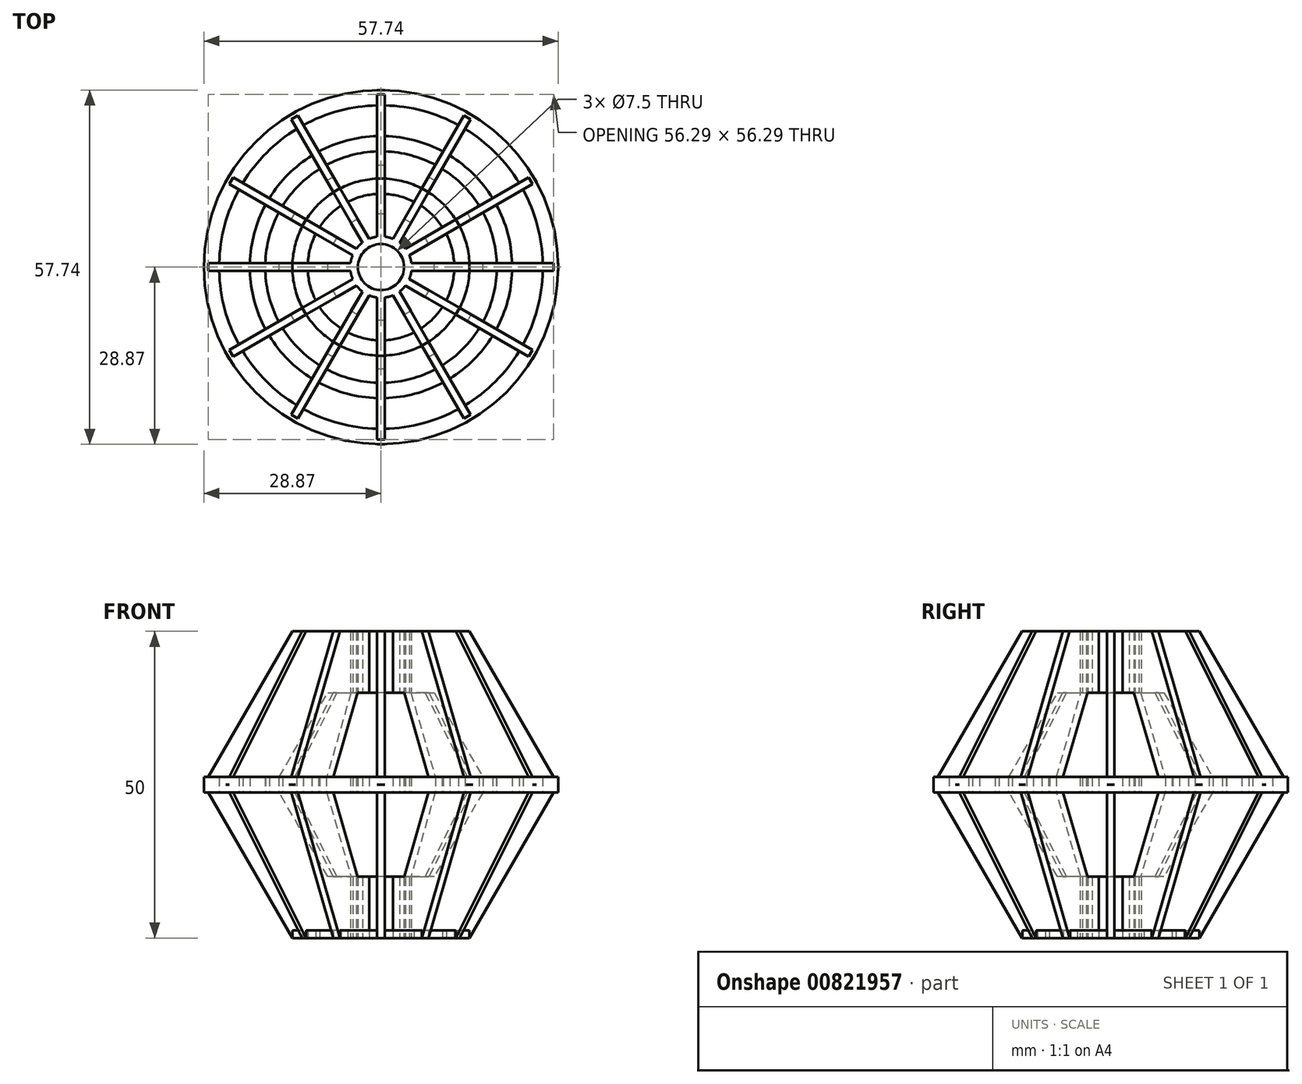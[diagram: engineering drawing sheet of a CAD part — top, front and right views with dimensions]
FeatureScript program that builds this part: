
annotation { "Feature Type Name" : "Feature", "Feature Type Description" : "" }
export const myFeature = defineFeature(function(context is Context, id is Id, definition is map)
    precondition{}
    {
        {
            var Q0;
            Q0=qCreatedBy(makeId("Front.planeOp"),FACE);
            var sketch = newSketch(context, id + "F0", { "sketchPlane" : qUnion([Q0])});
            skCircle(sketch, "E0.cCircle", {"center": v(0, 0) * mm, "radius": 25 * mm, "construction": true});
            skLineSegment(sketch, "E0.0", {"start": v(-14.43, 25) * mm, "end": v(14.43, 25) * mm});
            skLineSegment(sketch, "E0.1", {"start": v(14.43, 25) * mm, "end": v(28.87, 0) * mm});
            skLineSegment(sketch, "E0.2", {"start": v(28.87, 0) * mm, "end": v(14.43, -25) * mm});
            skLineSegment(sketch, "E0.3", {"start": v(14.43, -25) * mm, "end": v(-14.43, -25) * mm});
            skLineSegment(sketch, "E0.4", {"start": v(-14.43, -25) * mm, "end": v(-28.87, 0) * mm});
            skLineSegment(sketch, "E0.5", {"start": v(-28.87, 0) * mm, "end": v(-14.43, 25) * mm});
            skPoint(sketch, "E0.0.midPoint", {"position": v(0, 25) * mm});
            skLineSegment(sketch, "E1", {"start": v(0, 0) * mm, "end": v(0, 13.52) * mm, "construction": true});
            skPoint(sketch, "E2.0.midPoint", {"position": v(0, 13.52) * mm});
            skCircle(sketch, "E3.cCircle", {"center": v(0, 0) * mm, "radius": 15 * mm, "construction": true});
            skLineSegment(sketch, "E3.0", {"start": v(-8.66, 15) * mm, "end": v(8.66, 15) * mm});
            skLineSegment(sketch, "E3.1", {"start": v(8.66, 15) * mm, "end": v(17.32, 0) * mm});
            skLineSegment(sketch, "E3.2", {"start": v(17.32, 0) * mm, "end": v(8.66, -15) * mm});
            skLineSegment(sketch, "E3.3", {"start": v(8.66, -15) * mm, "end": v(-8.66, -15) * mm});
            skLineSegment(sketch, "E3.4", {"start": v(-8.66, -15) * mm, "end": v(-17.32, 0) * mm});
            skLineSegment(sketch, "E3.5", {"start": v(-17.32, 0) * mm, "end": v(-8.66, 15) * mm});
            skPoint(sketch, "E3.0.midPoint", {"position": v(0, 15) * mm});
            skLineSegment(sketch, "E4.bottom", {"start": v(-28.15, -1.25) * mm, "end": v(28.15, -1.25) * mm});
            skLineSegment(sketch, "E4.top", {"start": v(-28.15, 1.25) * mm, "end": v(28.15, 1.25) * mm});
            skLineSegment(sketch, "E4.left", {"start": v(-28.15, -1.25) * mm, "end": v(-28.15, 1.25) * mm});
            skLineSegment(sketch, "E4.right", {"start": v(28.15, -1.25) * mm, "end": v(28.15, 1.25) * mm});
            skSolve(sketch);
        }
        {
            var Q0;
            Q0=makeQuery(id+"F0.imprint","IMPRINT",FACE,{"disambiguationData":[TD([[makeQuery(id+"F0.imprint","IMPRINT",EDGE,{"derivedFrom":sQuery(id+"F0.wireOp",EDGE,"E0.0")}),-1.0]])]});
            var Q1;
            {var subQ1=sQuery(id+"F0.wireOp",EDGE,"E0.3");Q1=makeQuery(id+"F0.imprint","IMPRINT",FACE,{"disambiguationData":[TD([[makeQuery(id+"F0.imprint","IMPRINT",EDGE,{"derivedFrom":subQ1}),-1.0]])]});}
            var Q2;
            {var subQ3=sQuery(id+"F0.wireOp",EDGE,"E4.left");Q2=makeQuery(id+"F0.imprint","IMPRINT",FACE,{"disambiguationData":[TD([[makeQuery(id+"F0.imprint","IMPRINT",EDGE,{"derivedFrom":subQ3}),1.0]])]});}
            var Q3;
            {var subQ0=sQuery(id+"F0.wireOp",EDGE,"E4.left");Q3=makeQuery(id+"F0.imprint","IMPRINT",FACE,{"disambiguationData":[TD([[makeQuery(id+"F0.imprint","IMPRINT",EDGE,{"derivedFrom":subQ0}),-1.0]])]});}
            var Q4;
            {var subQ0=sQuery(id+"F0.wireOp",EDGE,"E4.right");Q4=makeQuery(id+"F0.imprint","IMPRINT",FACE,{"disambiguationData":[TD([[makeQuery(id+"F0.imprint","IMPRINT",EDGE,{"derivedFrom":subQ0}),1.0]])]});}
            var Q5;
            {var subQ3=sQuery(id+"F0.wireOp",EDGE,"E4.right");Q5=makeQuery(id+"F0.imprint","IMPRINT",FACE,{"disambiguationData":[TD([[makeQuery(id+"F0.imprint","IMPRINT",EDGE,{"derivedFrom":subQ3}),-1.0]])]});}
            var Q6;
            {var subQ5=sQuery(id+"F0.wireOp",EDGE,"E3.2");var subQ6=sQuery(id+"F0.wireOp",EDGE,"E3.1");var subQ7=makeQuery(id+"F0.imprint","INTERSECT",VERTEX,{"derivedFrom":[subQ6,subQ5]});Q6=makeQuery(id+"F0.imprint","IMPRINT",FACE,{"disambiguationData":[TD([[makeQuery(id+"F0.imprint","IMPRINT",EDGE,{"disambiguationData":[TD([[subQ7,1.0]])],"derivedFrom":subQ6}),-1.0]])]});}
            extrude(context, id + "F1", {"entities" : qUnion([Q0, Q1, Q2, Q3, Q4, Q5, Q6]), "endBound" : BoundingType.SYMMETRIC, "depth" : 1.25 * mm, "offsetDistance" : 25 * mm});
        }
        {
            var Q0;
            Q0=makeQuery(id+"F1.opExtrude","SWEPT_BODY",BODY,{"disambiguationData":[OSD([sQuery(id+"F0.wireOp",EDGE,"E0.0"),sQuery(id+"F0.wireOp",EDGE,"E0.1"),sQuery(id+"F0.wireOp",EDGE,"E0.2"),sQuery(id+"F0.wireOp",EDGE,"E0.3"),sQuery(id+"F0.wireOp",EDGE,"E0.4"),sQuery(id+"F0.wireOp",EDGE,"E0.5")])]});
            var Q1;
            Q1=sQuery(id+"F0.wireOp",EDGE,"E1");
            circularPattern(context, id + "F2", {"operationType" : NewBodyOperationType.ADD, "entities" : qUnion([Q0]), "axis" : qUnion([Q1]), "angle" : 360 * degree, "instanceCount" : 12, "equalSpace" : true});
        }
        {
            var Q0;
            Q0=qCreatedBy(makeId("Top.planeOp"),FACE);
            var sketch = newSketch(context, id + "F3", { "sketchPlane" : qUnion([Q0])});
            skCircle(sketch, "E5", {"center": v(0, 0) * mm, "radius": 5 * mm});
            skCircle(sketch, "E6", {"center": v(0, 0) * mm, "radius": 3.75 * mm});
            skCircle(sketch, "E7", {"center": v(0, 0) * mm, "radius": 28.87 * mm});
            skCircle(sketch, "E8", {"center": v(0, 0) * mm, "radius": 26.37 * mm});
            skCircle(sketch, "E9", {"center": v(0, 0) * mm, "radius": 21.37 * mm});
            skCircle(sketch, "E10", {"center": v(0, 0) * mm, "radius": 18.87 * mm});
            skSolve(sketch);
        }
        {
            var Q0;
            Q0=makeQuery(id+"F3.imprint","IMPRINT",FACE,{"disambiguationData":[TD([[makeQuery(id+"F3.imprint","IMPRINT",EDGE,{"derivedFrom":sQuery(id+"F3.wireOp",EDGE,"E5")}),1.0]])]});
            extrude(context, id + "F4", {"entities" : qUnion([Q0]), "operationType" : NewBodyOperationType.ADD, "endBound" : BoundingType.SYMMETRIC, "depth" : 50 * mm, "offsetDistance" : 25 * mm});
        }
        {
            var Q0;
            Q0=makeQuery(id+"F3.imprint","IMPRINT",FACE,{"disambiguationData":[TD([[makeQuery(id+"F3.imprint","IMPRINT",EDGE,{"derivedFrom":sQuery(id+"F3.wireOp",EDGE,"E5")}),1.0]])]});
            var Q1;
            Q1=sQuery(id+"F3.wireOp",EDGE,"E5");
            var Q2;
            Q2=sQuery(id+"F3.wireOp",EDGE,"E6");
            extrude(context, id + "F5", {"entities" : qUnion([Q0]), "operationType" : NewBodyOperationType.REMOVE, "surfaceEntities" : qUnion([Q1, Q2]), "endBound" : BoundingType.SYMMETRIC, "depth" : 30 * mm, "offsetDistance" : 25 * mm});
        }
        {
            var Q0;
            Q0 = qSketchRegion(id + "F3", true);
            var Q1;
            Q1=makeQuery(id+"F3.imprint","IMPRINT",FACE,{"disambiguationData":[TD([[makeQuery(id+"F3.imprint","IMPRINT",EDGE,{"derivedFrom":sQuery(id+"F3.wireOp",EDGE,"E9")}),1.0]])]});
            extrude(context, id + "F6", {"entities" : qUnion([Q0, Q1]), "operationType" : NewBodyOperationType.ADD, "endBound" : BoundingType.SYMMETRIC, "depth" : 2.5 * mm, "offsetDistance" : 25 * mm});
        }
        {
            var Q0;
            {var subQ0=makeQuery(id+"F1.opExtrude","SWEPT_FACE",FACE,{"disambiguationData":[OSD([sQuery(id+"F0.wireOp",EDGE,"E0.3")])]});Q0=makeQuery(id+"F4.boolean.opBoolean","MERGE",FACE,{"derivedFrom":[makeQuery(id+"F2.boolean.opBoolean","MERGE",FACE,{"derivedFrom":[subQ0,makeQuery(id+"F2.opPattern","COPY",FACE,{"derivedFrom":subQ0,"instanceName":"1"}),makeQuery(id+"F2.opPattern","COPY",FACE,{"derivedFrom":subQ0,"instanceName":"2"}),makeQuery(id+"F2.opPattern","COPY",FACE,{"derivedFrom":subQ0,"instanceName":"3"}),makeQuery(id+"F2.opPattern","COPY",FACE,{"derivedFrom":subQ0,"instanceName":"4"}),makeQuery(id+"F2.opPattern","COPY",FACE,{"derivedFrom":subQ0,"instanceName":"5"}),makeQuery(id+"F2.opPattern","COPY",FACE,{"derivedFrom":subQ0,"instanceName":"6"}),makeQuery(id+"F2.opPattern","COPY",FACE,{"derivedFrom":subQ0,"instanceName":"7"})]}),makeQuery(id+"F4.opExtrude","CAP_FACE",FACE,{"disambiguationData":[OSD([sQuery(id+"F3.wireOp",EDGE,"E5"),sQuery(id+"F3.wireOp",EDGE,"E6")])],"isStart":true})]});}
            var sketch = newSketch(context, id + "F7", { "sketchPlane" : qUnion([Q0])});
            skCircle(sketch, "E11", {"center": v(0, 0) * mm, "radius": 14.43 * mm});
            skCircle(sketch, "E12", {"center": v(0, 0) * mm, "radius": 11.93 * mm});
            skSolve(sketch);
        }
        {
            var Q0;
            Q0 = qSketchRegion(id + "F7", true);
            extrude(context, id + "F8", {"entities" : qUnion([Q0]), "operationType" : NewBodyOperationType.ADD, "oppositeDirection" : true, "depth" : 1.25 * mm, "offsetDistance" : 25 * mm});
        }
        {
            var Q0;
            Q0=makeQuery(id+"F3.imprint","IMPRINT",FACE,{"disambiguationData":[TD([[makeQuery(id+"F3.imprint","IMPRINT",EDGE,{"derivedFrom":sQuery(id+"F3.wireOp",EDGE,"E6")}),1.0]])]});
            extrude(context, id + "F9", {"entities" : qUnion([Q0]), "operationType" : NewBodyOperationType.REMOVE, "endBound" : BoundingType.SYMMETRIC, "oppositeDirection" : true, "depth" : 50 * mm, "offsetDistance" : 25 * mm});
        }
        {
            var Q0;
            Q0=makeQuery(id+"F3.imprint","IMPRINT",FACE,{"disambiguationData":[TD([[makeQuery(id+"F3.imprint","IMPRINT",EDGE,{"derivedFrom":sQuery(id+"F3.wireOp",EDGE,"E5")}),1.0]])]});
            extrude(context, id + "F10", {"entities" : qUnion([Q0]), "operationType" : NewBodyOperationType.ADD, "endBound" : BoundingType.SYMMETRIC, "depth" : 2.5 * mm, "offsetDistance" : 25 * mm});
        }
    });
